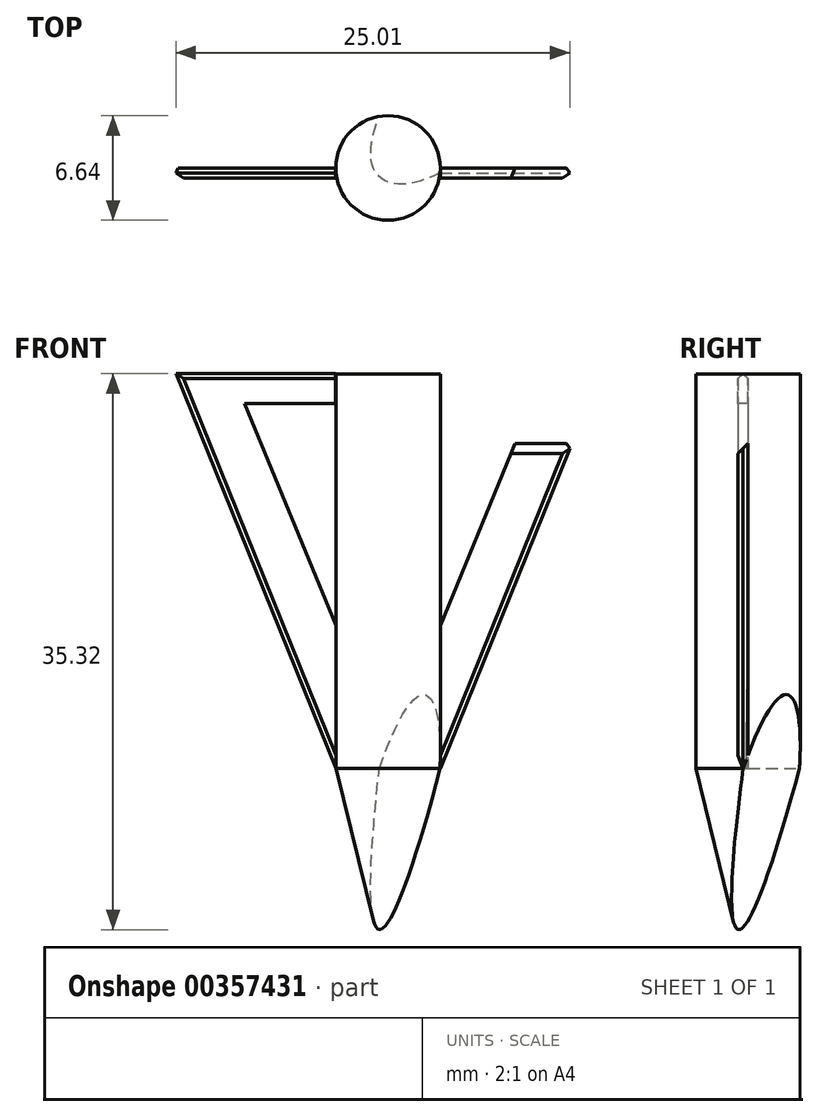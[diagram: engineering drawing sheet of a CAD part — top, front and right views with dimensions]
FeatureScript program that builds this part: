
annotation { "Feature Type Name" : "Feature", "Feature Type Description" : "" }
export const myFeature = defineFeature(function(context is Context, id is Id, definition is map)
    precondition{}
    {
        {
            var Q0;
            Q0=qCreatedBy(makeId("Front.planeOp"),FACE);
            var sketch = newSketch(context, id + "F0", { "sketchPlane" : qUnion([Q0])});
            skLineSegment(sketch, "E0.bottom", {"start": v(0, 0) * mm, "end": v(3.32, 0) * mm});
            skLineSegment(sketch, "E0.top", {"start": v(0, 25.07) * mm, "end": v(3.32, 25.07) * mm});
            skLineSegment(sketch, "E0.left", {"start": v(0, 0) * mm, "end": v(0, 25.07) * mm});
            skLineSegment(sketch, "E0.right", {"start": v(3.32, 0) * mm, "end": v(3.32, 25.07) * mm});
            skLineSegment(sketch, "E1", {"start": v(3.32, 0) * mm, "end": v(0, -13.46) * mm});
            skLineSegment(sketch, "E2", {"start": v(0, -13.46) * mm, "end": v(0, 0) * mm});
            skSolve(sketch);
        }
        {
            var Q0;
            Q0=makeQuery(id+"F0.imprint","IMPRINT",FACE,{"disambiguationData":[TD([[makeQuery(id+"F0.imprint","IMPRINT",EDGE,{"derivedFrom":sQuery(id+"F0.wireOp",EDGE,"E0.bottom")}),1.0]])]});
            var Q1;
            Q1=makeQuery(id+"F0.imprint","IMPRINT",FACE,{"disambiguationData":[TD([[makeQuery(id+"F0.imprint","IMPRINT",EDGE,{"derivedFrom":sQuery(id+"F0.wireOp",EDGE,"E0.bottom")}),-1.0]])]});
            var Q2;
            Q2=sQuery(id+"F0.wireOp",EDGE,"E0.left");
            revolve(context, id + "F1", {"entities" : qUnion([Q0, Q1]), "axis" : qUnion([Q2]), "revolveType" : RevolveType.FULL});
        }
        {
            var Q0;
            Q0=qCreatedBy(makeId("Front.planeOp"),FACE);
            var sketch = newSketch(context, id + "F2", { "sketchPlane" : qUnion([Q0])});
            skLineSegment(sketch, "E3", {"start": v(3.32, 25.08) * mm, "end": v(13.47, 25.08) * mm});
            skLineSegment(sketch, "E4", {"start": v(13.47, 25.08) * mm, "end": v(3.32, 0) * mm});
            skLineSegment(sketch, "E5", {"start": v(3.32, 0) * mm, "end": v(3.32, 25.08) * mm});
            skLineSegment(sketch, "E6.MirrorCS", {"start": v(-3.32, 0) * mm, "end": v(-3.32, 25.08) * mm});
            skLineSegment(sketch, "E7.MirrorCS", {"start": v(-3.32, 25.08) * mm, "end": v(-13.47, 25.08) * mm});
            skLineSegment(sketch, "E8.MirrorCS", {"start": v(-13.47, 25.08) * mm, "end": v(-3.32, 0) * mm});
            skSolve(sketch);
        }
        {
            var Q0;
            Q0=makeQuery(id+"F2.imprint","IMPRINT",FACE,{"disambiguationData":[TD([[makeQuery(id+"F2.imprint","IMPRINT",EDGE,{"derivedFrom":sQuery(id+"F2.wireOp",EDGE,"E6.MirrorCS")}),1.0]])]});
            var Q1;
            Q1=makeQuery(id+"F2.imprint","IMPRINT",FACE,{"disambiguationData":[TD([[makeQuery(id+"F2.imprint","IMPRINT",EDGE,{"derivedFrom":sQuery(id+"F2.wireOp",EDGE,"E3")}),-1.0]])]});
            extrude(context, id + "F3", {"entities" : qUnion([Q0, Q1]), "operationType" : NewBodyOperationType.ADD, "depth" : 0.64 * mm});
        }
        {
            var Q0;
            Q0=makeQuery(id+"F3.opExtrude","CAP_FACE",FACE,{"disambiguationData":[OSD([sQuery(id+"F2.wireOp",EDGE,"E6.MirrorCS"),sQuery(id+"F2.wireOp",EDGE,"E7.MirrorCS"),sQuery(id+"F2.wireOp",EDGE,"E8.MirrorCS")])],"isStart":false});
            var sketch = newSketch(context, id + "F4", { "sketchPlane" : qUnion([Q0])});
            skLineSegment(sketch, "E9", {"start": v(-3.32, 23.19) * mm, "end": v(-9.12, 23.19) * mm});
            skLineSegment(sketch, "E10", {"start": v(-9.12, 23.19) * mm, "end": v(-3.32, 9.08) * mm});
            skLineSegment(sketch, "E11", {"start": v(-3.32, 9.08) * mm, "end": v(-3.32, 23.19) * mm});
            skLineSegment(sketch, "E12.MirrorCS", {"start": v(3.32, 9.08) * mm, "end": v(3.32, 23.19) * mm});
            skLineSegment(sketch, "E13.MirrorCS", {"start": v(3.32, 23.19) * mm, "end": v(9.12, 23.19) * mm});
            skLineSegment(sketch, "E14.MirrorCS", {"start": v(9.12, 23.19) * mm, "end": v(3.32, 9.08) * mm});
            skSolve(sketch);
        }
        {
            var Q0;
            Q0=makeQuery(id+"F4.imprint","IMPRINT",FACE,{"disambiguationData":[TD([[makeQuery(id+"F4.imprint","IMPRINT",EDGE,{"derivedFrom":sQuery(id+"F4.wireOp",EDGE,"E9")}),1.0]])]});
            var Q1;
            Q1=makeQuery(id+"F4.imprint","IMPRINT",FACE,{"disambiguationData":[TD([[makeQuery(id+"F4.imprint","IMPRINT",EDGE,{"derivedFrom":sQuery(id+"F4.wireOp",EDGE,"E12.MirrorCS")}),-1.0]])]});
            extrude(context, id + "F5", {"entities" : qUnion([Q0, Q1]), "operationType" : NewBodyOperationType.REMOVE, "oppositeDirection" : true, "depth" : 0.66 * mm});
        }
        {
            var Q0;
            Q0=makeQuery(id+"F3.opExtrude","CAP_EDGE",EDGE,{"disambiguationData":[OSD([sQuery(id+"F2.wireOp",EDGE,"E3")])],"isStart":false});
            chamfer(context, id + "F6", {"entities" : qUnion([Q0]), "width" : 5.08 * mm, "tangentPropagation" : true});
        }
        {
            var Q0;
            Q0=makeQuery(id+"F3.opExtrude","CAP_EDGE",EDGE,{"disambiguationData":[OSD([sQuery(id+"F2.wireOp",EDGE,"E3")])],"isStart":false});
            var Q1;
            Q1=makeQuery(id+"F3.opExtrude","CAP_EDGE",EDGE,{"disambiguationData":[OSD([sQuery(id+"F2.wireOp",EDGE,"E7.MirrorCS")])],"isStart":false});
            chamfer(context, id + "F7", {"entities" : qUnion([Q0, Q1]), "width" : 0.32 * mm, "tangentPropagation" : true});
        }
        {
            var Q0;
            Q0=makeQuery(id+"F3.opExtrude","CAP_EDGE",EDGE,{"disambiguationData":[OSD([sQuery(id+"F2.wireOp",EDGE,"E3")])],"isStart":true});
            var Q1;
            Q1=makeQuery(id+"F3.opExtrude","CAP_EDGE",EDGE,{"disambiguationData":[OSD([sQuery(id+"F2.wireOp",EDGE,"E7.MirrorCS")])],"isStart":true});
            chamfer(context, id + "F8", {"entities" : qUnion([Q0, Q1]), "width" : 0.32 * mm, "tangentPropagation" : true});
        }
        {
            var Q0;
            Q0=makeQuery(id+"F3.opExtrude","CAP_EDGE",EDGE,{"disambiguationData":[OSD([sQuery(id+"F2.wireOp",EDGE,"E4")])],"isStart":false});
            var Q1;
            Q1=makeQuery(id+"F3.opExtrude","CAP_EDGE",EDGE,{"disambiguationData":[OSD([sQuery(id+"F2.wireOp",EDGE,"E4")])],"isStart":true});
            var Q2;
            Q2=makeQuery(id+"F3.opExtrude","CAP_EDGE",EDGE,{"disambiguationData":[OSD([sQuery(id+"F2.wireOp",EDGE,"E8.MirrorCS")])],"isStart":false});
            chamfer(context, id + "F9", {"entities" : qUnion([Q0, Q1, Q2]), "width" : 0.32 * mm, "tangentPropagation" : true});
        }
    });
